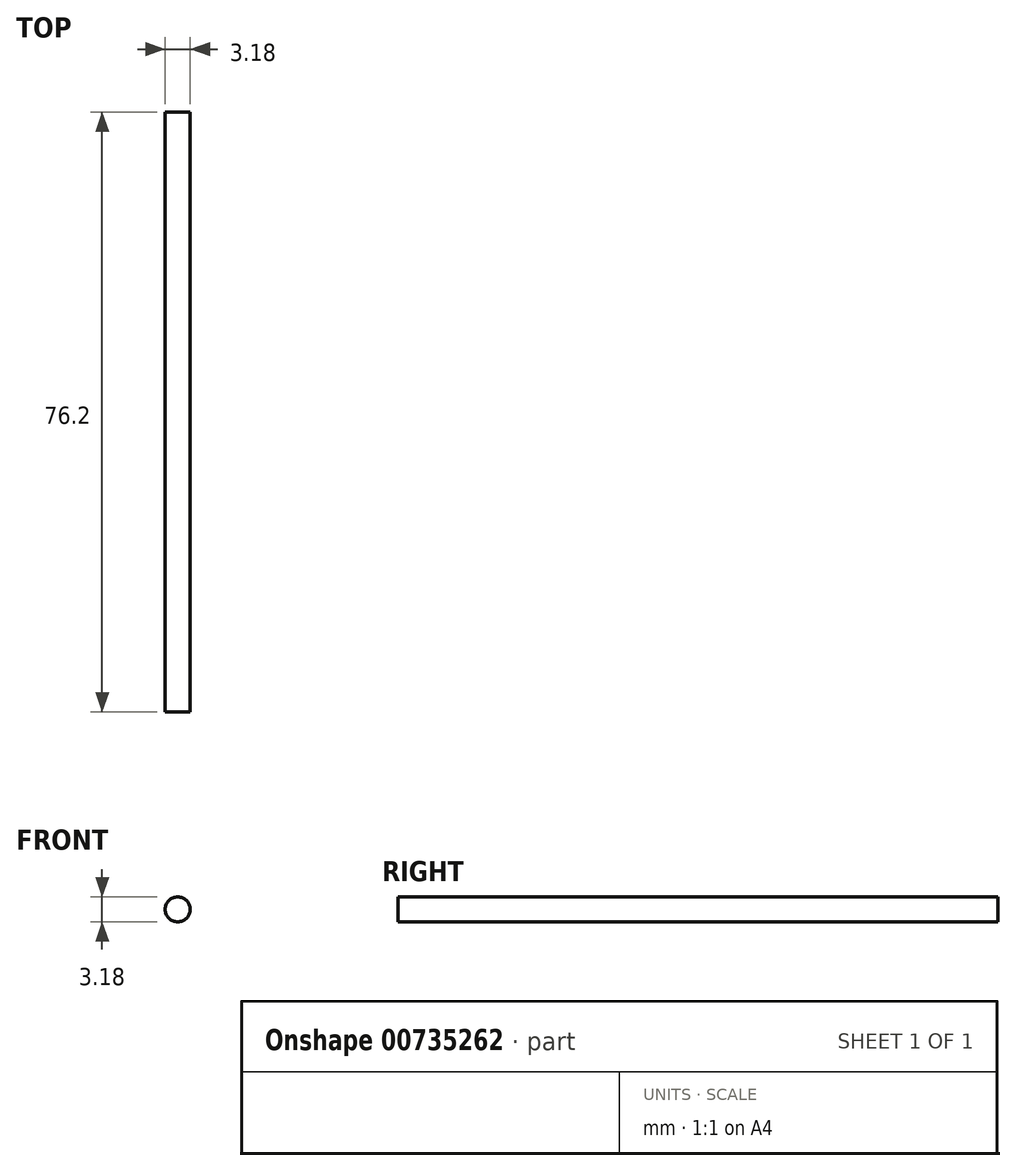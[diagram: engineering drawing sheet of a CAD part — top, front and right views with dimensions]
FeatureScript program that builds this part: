
annotation { "Feature Type Name" : "Feature", "Feature Type Description" : "" }
export const myFeature = defineFeature(function(context is Context, id is Id, definition is map)
    precondition{}
    {
        {
            var Q0;
            Q0=qCreatedBy(makeId("Front.planeOp"),FACE);
            var sketch = newSketch(context, id + "F0", { "sketchPlane" : qUnion([Q0])});
            skCircle(sketch, "E0", {"center": v(0, 0) * mm, "radius": 1.59 * mm});
            skSolve(sketch);
        }
        {
            var Q0;
            Q0=makeQuery(id+"F0.imprint","IMPRINT",FACE,{"disambiguationData":[TD([[makeQuery(id+"F0.imprint","IMPRINT",EDGE,{"derivedFrom":sQuery(id+"F0.wireOp",EDGE,"E0")}),1.0]])]});
            extrude(context, id + "F1", {"entities" : qUnion([Q0]), "depth" : 76.2 * mm, "offsetDistance" : 25.4 * mm});
        }
    });
